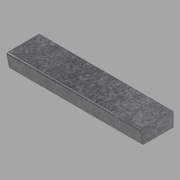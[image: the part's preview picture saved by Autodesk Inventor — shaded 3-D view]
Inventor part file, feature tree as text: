
AUTODESK INVENTOR PART (.ipt)
format: ipt  version: 2022.1 (Build 261234020, 234B)  size: 99,328 bytes
history: native  units: in
note: dims shown in document units (in); Inventor stores cm internally (conversion verified against a paired STEP export)
features: other x3, extrude x1, sketch x1
ambient origin geometry x8: Origin, YZ Plane, XZ Plane, XY Plane, X Axis, Y Axis, Z Axis, Center Point
bodies: Solid1 (feature_tree)
feature tree (5):
  other  "Blocks"
  extrude  "Extrusion1"  Depth=57.9375in TaperAngle=0.0deg
  sketch  "Sketch1"  dims[d0=13.0in d1=6.0in d2=13.5in d3=0.5in d4=0.5in d5=57.9375in d6=0.0in]
  other  "Profile"
  other  "Profile:1"
